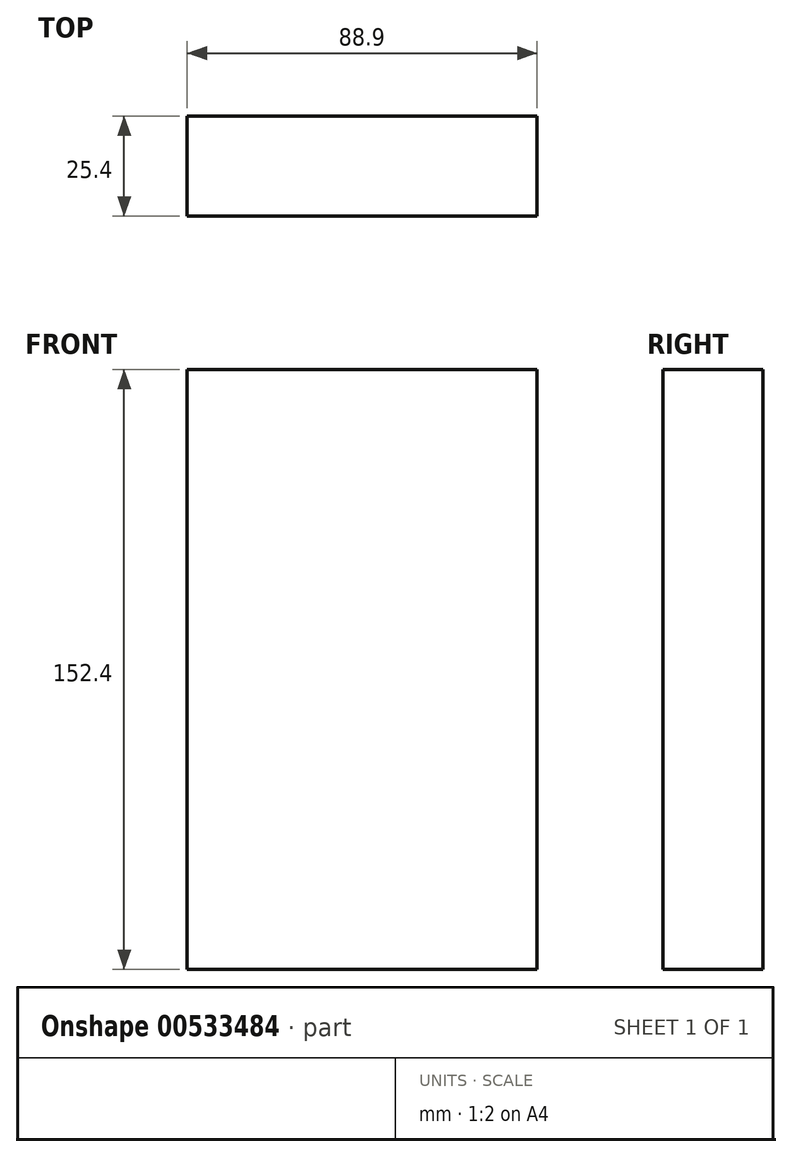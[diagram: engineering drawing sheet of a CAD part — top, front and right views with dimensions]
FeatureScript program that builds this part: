
annotation { "Feature Type Name" : "Feature", "Feature Type Description" : "" }
export const myFeature = defineFeature(function(context is Context, id is Id, definition is map)
    precondition{}
    {
        {
            var Q0;
            Q0=qCreatedBy(makeId("Front.planeOp"),FACE);
            var sketch = newSketch(context, id + "F0", { "sketchPlane" : qUnion([Q0])});
            skLineSegment(sketch, "E0.bottom", {"start": v(-48.37, 71.66) * mm, "end": v(40.53, 71.66) * mm});
            skLineSegment(sketch, "E0.top", {"start": v(-48.37, -80.74) * mm, "end": v(40.53, -80.74) * mm});
            skLineSegment(sketch, "E0.left", {"start": v(-48.37, 71.66) * mm, "end": v(-48.37, -80.74) * mm});
            skLineSegment(sketch, "E0.right", {"start": v(40.53, 71.66) * mm, "end": v(40.53, -80.74) * mm});
            skSolve(sketch);
        }
        {
            var Q0;
            Q0 = qSketchRegion(id + "F0", true);
            extrude(context, id + "F1", {"entities" : qUnion([Q0]), "depth" : 25.4 * mm, "offsetDistance" : 25.4 * mm});
        }
    });
